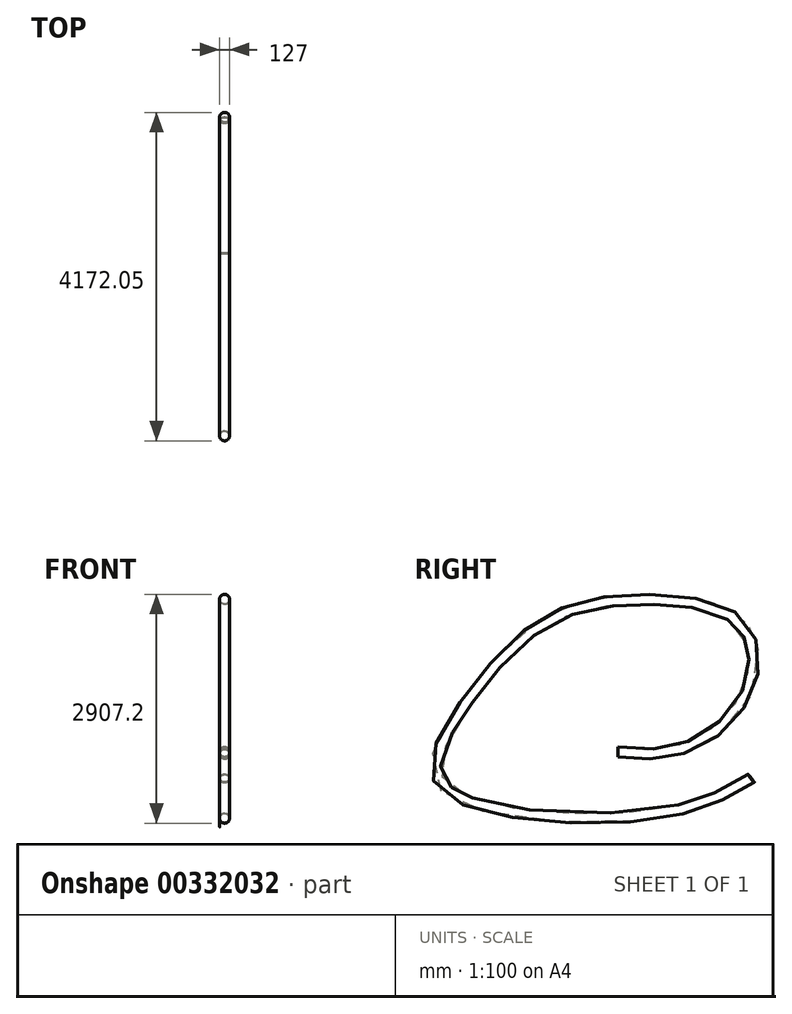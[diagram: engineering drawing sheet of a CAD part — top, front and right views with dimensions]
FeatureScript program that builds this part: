
annotation { "Feature Type Name" : "Feature", "Feature Type Description" : "" }
export const myFeature = defineFeature(function(context is Context, id is Id, definition is map)
    precondition{}
    {
        {
            var Q0;
            Q0=qCreatedBy(makeId("Front.planeOp"),FACE);
            var sketch = newSketch(context, id + "F0", { "sketchPlane" : qUnion([Q0])});
            skCircle(sketch, "E0", {"center": v(0, 0) * mm, "radius": 63.5 * mm});
            skSolve(sketch);
        }
        {
            var Q0;
            Q0=qCreatedBy(makeId("Right.planeOp"),FACE);
            var sketch = newSketch(context, id + "F1", { "sketchPlane" : qUnion([Q0])});
            skFitSpline(sketch, "E1", {"points": [v(0, 0) * mm, v(660.04, 0) * mm, v(1411.56, 419.56) * mm, v(1726.33, 1131.32) * mm, v(1474.17, 1703.3) * mm, v(320.21, 1938.95) * mm, v(-868.39, 1687.56) * mm, v(-1877.3, 703.6) * mm, v(-2301.45, -308.46) * mm, v(-1297.55, -774.55) * mm, v(802.13, -729.74) * mm, v(1691.18, -335.33) * mm], "startDerivative": vector(8961.48, -1014.73) * mm, "endDerivative": vector(8703.87, 5200.1) * mm});
            skSolve(sketch);
        }
        {
            var Q0;
            Q0=makeQuery(id+"F0.imprint","IMPRINT",FACE,{"disambiguationData":[TD([[makeQuery(id+"F0.imprint","IMPRINT",EDGE,{"derivedFrom":sQuery(id+"F0.wireOp",EDGE,"E0")}),1.0]])]});
            var Q1;
            Q1=sQuery(id+"F1.wireOp",EDGE,"E1");
            sweep(context, id + "F2", {"profiles" : qUnion([Q0]), "path" : qUnion([Q1])});
        }
        {
            var Q0;
            Q0=makeQuery(id+"F2.opSweep","CAP_FACE",FACE,{"disambiguationData":[OSD([sQuery(id+"F0.wireOp",EDGE,"E0"),sQuery(id+"F1.wireOp",VERTEX,"E1.end")])],"isStart":false});
            shell(context, id + "F3", {"entities" : qUnion([Q0]), "thickness" : 2.54 * mm});
        }
        {
            var Q0;
            Q0=makeQuery(id+"F2.opSweep","CAP_EDGE",EDGE,{"disambiguationData":[OSD([sQuery(id+"F0.wireOp",EDGE,"E0"),sQuery(id+"F1.wireOp",VERTEX,"E1.end")])],"isStart":false});
            fillet(context, id + "F4", {"entities" : qUnion([Q0]), "radius" : 5.08 * mm, "tangentPropagation" : true, "allowEdgeOverflow" : false});
        }
    });
